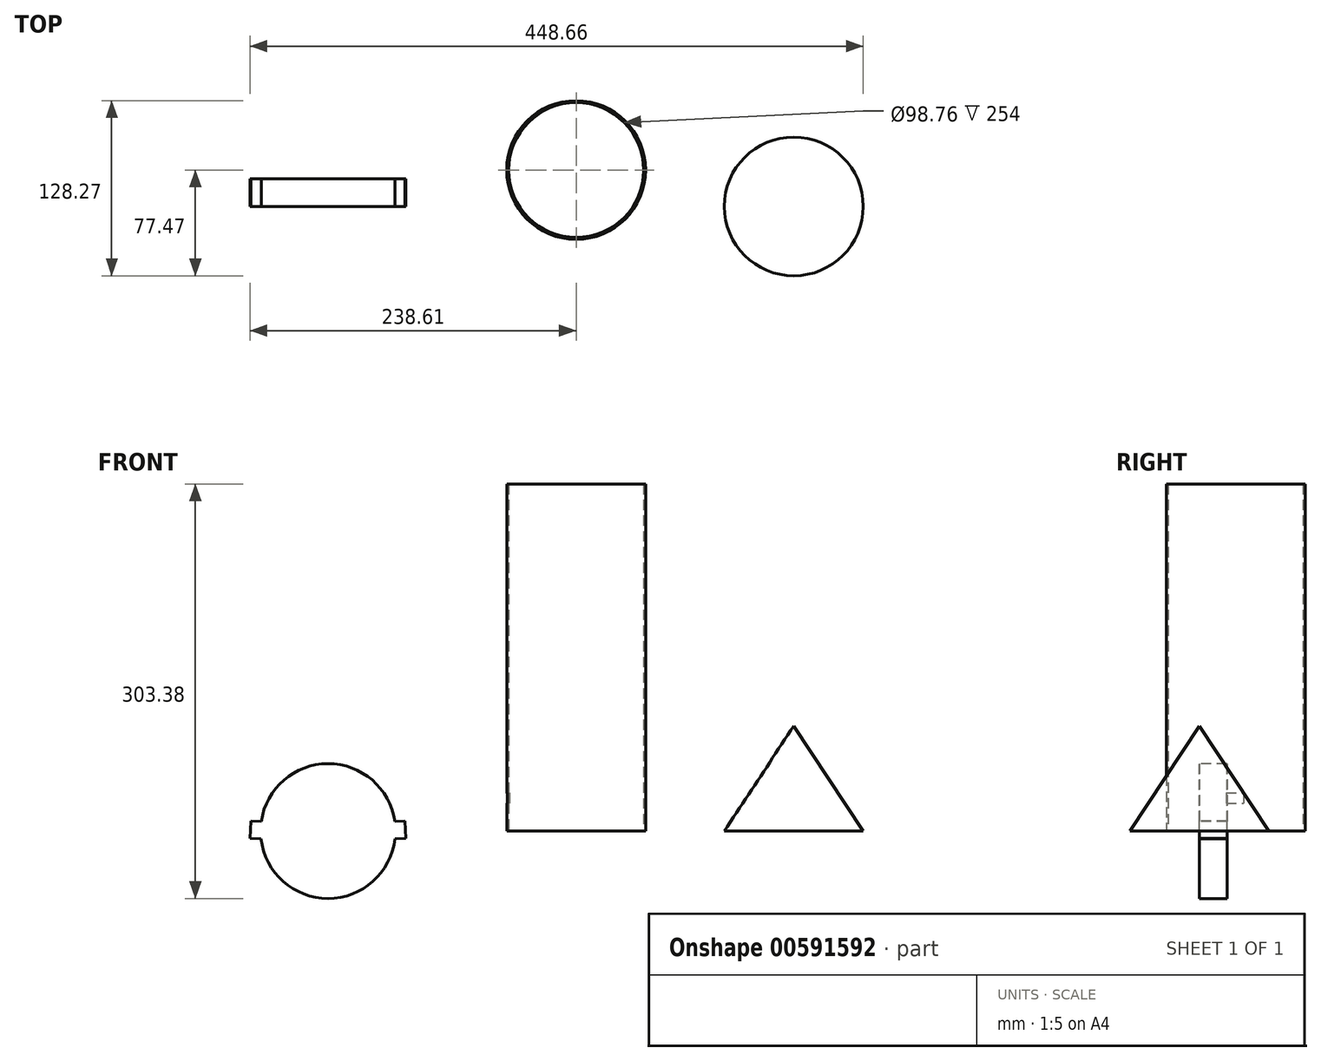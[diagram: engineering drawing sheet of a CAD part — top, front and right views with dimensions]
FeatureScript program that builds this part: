
annotation { "Feature Type Name" : "Feature", "Feature Type Description" : "" }
export const myFeature = defineFeature(function(context is Context, id is Id, definition is map)
    precondition{}
    {
        {
            var Q0;
            Q0=qCreatedBy(makeId("Top.planeOp"),FACE);
            var sketch = newSketch(context, id + "F0", { "sketchPlane" : qUnion([Q0])});
            skCircle(sketch, "E0", {"center": v(0, 26.67) * mm, "radius": 50.8 * mm});
            skCircle(sketch, "E1", {"center": v(0, 26.67) * mm, "radius": 49.38 * mm});
            skSolve(sketch);
        }
        {
            var Q0;
            Q0=makeQuery(id+"F0.imprint","IMPRINT",FACE,{"disambiguationData":[TD([[makeQuery(id+"F0.imprint","IMPRINT",EDGE,{"derivedFrom":sQuery(id+"F0.wireOp",EDGE,"E0")}),1.0]])]});
            extrude(context, id + "F1", {"entities" : qUnion([Q0]), "depth" : 254 * mm, "offsetDistance" : 25.4 * mm});
        }
        {
            var Q0;
            Q0=qCreatedBy(makeId("Front.planeOp"),FACE);
            var sketch = newSketch(context, id + "F2", { "sketchPlane" : qUnion([Q0])});
            skLineSegment(sketch, "E2", {"start": v(159.25, 76.96) * mm, "end": v(159.25, 0) * mm});
            skLineSegment(sketch, "E3", {"start": v(159.25, 0) * mm, "end": v(177.7, 0) * mm});
            skLineSegment(sketch, "E4", {"start": v(159.25, 76.96) * mm, "end": v(210.05, 0) * mm});
            skLineSegment(sketch, "E5.trimOffspring", {"start": v(191.6, 0) * mm, "end": v(210.05, 0) * mm});
            skLineSegment(sketch, "E6", {"start": v(177.7, 0) * mm, "end": v(191.6, 0) * mm});
            skArc(sketch, "E7", {"start": v(-230.6, -5.64) * mm, "mid": v(-181.55, -49.38) * mm, "end": v(-132.5, -5.64) * mm});
            skArc(sketch, "E8", {"start": v(-229.18, -5.7) * mm, "mid": v(-181.55, -47.97) * mm, "end": v(-133.93, -5.7) * mm});
            skLineSegment(sketch, "E9.bottom", {"start": v(-238.6, -5.29) * mm, "end": v(-238.04, 7.4) * mm});
            skLineSegment(sketch, "E9.left", {"start": v(-238.6, -5.29) * mm, "end": v(-230.6, -5.64) * mm});
            skLineSegment(sketch, "E9.right", {"start": v(-238.04, 7.4) * mm, "end": v(-230.43, 7.06) * mm});
            skLineSegment(sketch, "E10.MirrorCS", {"start": v(-125.19, 7.4) * mm, "end": v(-132.8, 7.06) * mm});
            skLineSegment(sketch, "E11.MirrorCS", {"start": v(-124.62, -5.29) * mm, "end": v(-125.19, 7.4) * mm});
            skLineSegment(sketch, "E12.MirrorCS", {"start": v(-124.62, -5.29) * mm, "end": v(-132.62, -5.64) * mm});
            skArc(sketch, "E13.trimOffspring", {"start": v(-132.69, 7.06) * mm, "mid": v(-181.56, 49.38) * mm, "end": v(-230.43, 7.06) * mm});
            skLineSegment(sketch, "E14", {"start": v(-132.5, -5.64) * mm, "end": v(-132.62, -5.64) * mm});
            skArc(sketch, "E15.trimOffspring", {"start": v(-134.11, 7.06) * mm, "mid": v(-181.6, 47.97) * mm, "end": v(-229.01, 7) * mm});
            skSolve(sketch);
        }
        {
            var Q0;
            Q0=makeQuery(id+"F2.imprint","IMPRINT",FACE,{"disambiguationData":[TD([[makeQuery(id+"F2.imprint","IMPRINT",EDGE,{"derivedFrom":sQuery(id+"F2.wireOp",EDGE,"E2")}),1.0]])]});
            var Q1;
            Q1=sQuery(id+"F2.wireOp",EDGE,"E2");
            revolve(context, id + "F3", {"operationType" : NewBodyOperationType.ADD, "entities" : qUnion([Q0]), "axis" : qUnion([Q1]), "revolveType" : RevolveType.FULL});
        }
        {
            var Q0;
            Q0=makeQuery(id+"F2.imprint","IMPRINT",FACE,{"disambiguationData":[TD([[makeQuery(id+"F2.imprint","IMPRINT",EDGE,{"derivedFrom":sQuery(id+"F2.wireOp",EDGE,"E7")}),1.0]])]});
            var Q1;
            Q1=sQuery(id+"F2.wireOp",EDGE,"E8");
            var Q2;
            Q2=sQuery(id+"F2.wireOp",EDGE,"E7");
            var Q3;
            Q3=sQuery(id+"F2.wireOp",EDGE,"E9.left");
            var Q4;
            Q4=sQuery(id+"F2.wireOp",EDGE,"E9.bottom");
            var Q5;
            Q5=sQuery(id+"F2.wireOp",EDGE,"E9.right");
            var Q6;
            Q6=sQuery(id+"F2.wireOp",EDGE,"E15.trimOffspring");
            var Q7;
            Q7=sQuery(id+"F2.wireOp",EDGE,"E13.trimOffspring");
            var Q8;
            Q8=sQuery(id+"F2.wireOp",EDGE,"E10.MirrorCS");
            var Q9;
            Q9=sQuery(id+"F2.wireOp",EDGE,"E11.MirrorCS");
            var Q10;
            Q10=sQuery(id+"F2.wireOp",EDGE,"E12.MirrorCS");
            extrude(context, id + "F4", {"entities" : qUnion([Q0]), "surfaceEntities" : qUnion([Q1, Q2, Q3, Q4, Q5, Q6, Q7, Q8, Q9, Q10]), "oppositeDirection" : true, "depth" : 20.32 * mm, "offsetDistance" : 25.4 * mm});
        }
        {
            var Q0;
            Q0=qCreatedBy(makeId("Right.planeOp"),FACE);
            var sketch = newSketch(context, id + "F5", { "sketchPlane" : qUnion([Q0])});
            skLineSegment(sketch, "E16.bottom", {"start": v(19.71, 27.87) * mm, "end": v(32.41, 27.87) * mm});
            skLineSegment(sketch, "E16.top", {"start": v(19.71, 20.25) * mm, "end": v(32.41, 20.25) * mm});
            skLineSegment(sketch, "E16.left", {"start": v(19.71, 27.87) * mm, "end": v(19.71, 20.25) * mm});
            skLineSegment(sketch, "E16.right", {"start": v(32.41, 27.87) * mm, "end": v(32.41, 20.25) * mm});
            skSolve(sketch);
        }
        {
            var Q0;
            Q0=makeQuery(id+"F5.imprint","IMPRINT",FACE,{"disambiguationData":[TD([[makeQuery(id+"F5.imprint","IMPRINT",EDGE,{"derivedFrom":sQuery(id+"F5.wireOp",EDGE,"E16.bottom")}),-1.0]])]});
            extrude(context, id + "F6", {"entities" : qUnion([Q0]), "operationType" : NewBodyOperationType.REMOVE, "oppositeDirection" : true, "depth" : 127 * mm, "offsetDistance" : 25.4 * mm});
        }
        {
            var Q0;
            Q0=qCreatedBy(makeId("Right.planeOp"),FACE);
            var sketch = newSketch(context, id + "F7", { "sketchPlane" : qUnion([Q0])});
            skLineSegment(sketch, "E17.top", {"start": v(76.72, 260.55) * mm, "end": v(143.8, 260.55) * mm});
            skLineSegment(sketch, "E17.left", {"start": v(76.72, 177.8) * mm, "end": v(76.72, 243.01) * mm});
            skLineSegment(sketch, "E18", {"start": v(76.72, 195.34) * mm, "end": v(143.8, 260.55) * mm});
            skSolve(sketch);
        }
        {
            var Q0;
            Q0=makeQuery(id+"F7.imprint","IMPRINT",FACE,{"disambiguationData":[TD([[makeQuery(id+"F7.imprint","IMPRINT",EDGE,{"derivedFrom":sQuery(id+"F7.wireOp",EDGE,"E17.top")}),-1.0]])]});
            var Q1;
            Q1=makeQuery(id+"F0.imprint","IMPRINT",FACE,{"disambiguationData":[TD([[makeQuery(id+"F0.imprint","IMPRINT",EDGE,{"derivedFrom":sQuery(id+"F0.wireOp",EDGE,"E1")}),1.0]])]});
            var Q2;
            Q2=sQuery(id+"F7.wireOp",EDGE,"E18");
            var Q3;
            Q3=sQuery(id+"F7.wireOp",EDGE,"E17.top");
            var Q4;
            Q4=sQuery(id+"F7.wireOp",EDGE,"E17.left");
            extrude(context, id + "F8", {"entities" : qUnion([Q0, Q1]), "operationType" : NewBodyOperationType.REMOVE, "surfaceEntities" : qUnion([Q2, Q3, Q4]), "depth" : 12.7 * mm, "offsetDistance" : 25.4 * mm});
        }
    });
